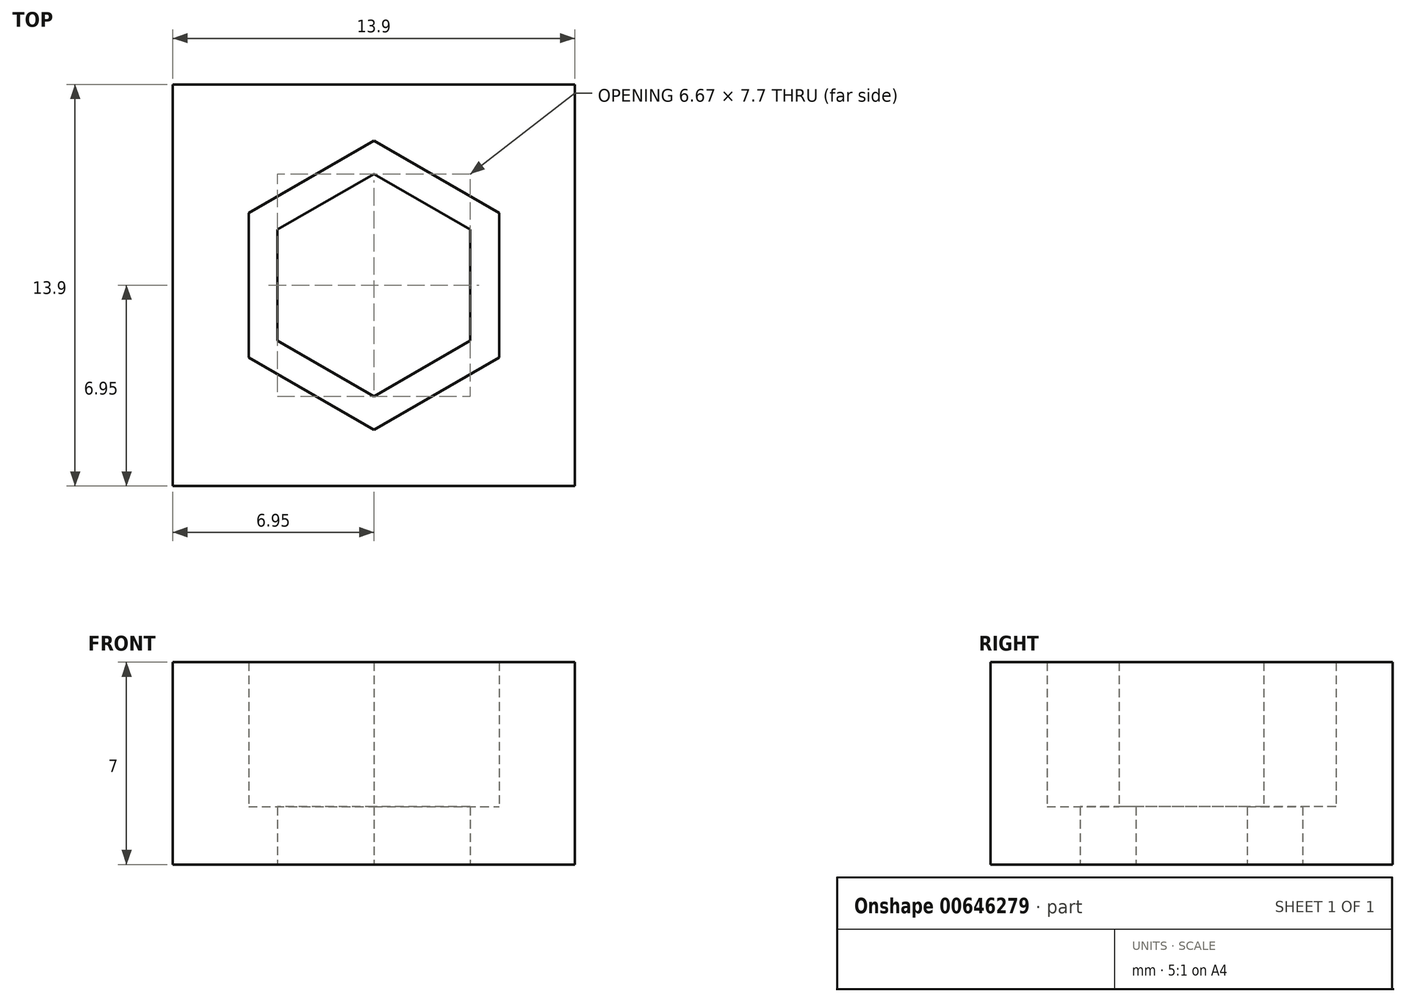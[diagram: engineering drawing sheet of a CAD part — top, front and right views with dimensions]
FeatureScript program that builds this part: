
annotation { "Feature Type Name" : "Feature", "Feature Type Description" : "" }
export const myFeature = defineFeature(function(context is Context, id is Id, definition is map)
    precondition{}
    {
        {
            var Q0;
            Q0=qCreatedBy(makeId("Top.planeOp"),FACE);
            var sketch = newSketch(context, id + "F0", { "sketchPlane" : qUnion([Q0])});
            skCircle(sketch, "E0", {"center": v(0, 0) * mm, "radius": 3.85 * mm});
            skLineSegment(sketch, "E1.bottom", {"start": v(6.95, 6.95) * mm, "end": v(-6.95, 6.95) * mm});
            skLineSegment(sketch, "E1.top", {"start": v(6.95, -6.95) * mm, "end": v(-6.95, -6.95) * mm});
            skLineSegment(sketch, "E1.left", {"start": v(6.95, 6.95) * mm, "end": v(6.95, -6.95) * mm});
            skLineSegment(sketch, "E1.right", {"start": v(-6.95, 6.95) * mm, "end": v(-6.95, -6.95) * mm});
            skCircle(sketch, "E2.cCircle", {"center": v(0, 0) * mm, "radius": 3.85 * mm, "construction": true});
            skLineSegment(sketch, "E2.0", {"start": v(0, 3.85) * mm, "end": v(3.33, 1.92) * mm});
            skLineSegment(sketch, "E2.1", {"start": v(3.33, 1.92) * mm, "end": v(3.33, -1.93) * mm});
            skLineSegment(sketch, "E2.2", {"start": v(3.33, -1.93) * mm, "end": v(0, -3.85) * mm});
            skLineSegment(sketch, "E2.3", {"start": v(0, -3.85) * mm, "end": v(-3.33, -1.92) * mm});
            skLineSegment(sketch, "E2.4", {"start": v(-3.33, -1.92) * mm, "end": v(-3.33, 1.93) * mm});
            skLineSegment(sketch, "E2.5", {"start": v(-3.33, 1.93) * mm, "end": v(0, 3.85) * mm});
            skSolve(sketch);
        }
        {
            var Q0;
            Q0=makeQuery(id+"F0.imprint","IMPRINT",FACE,{"disambiguationData":[TD([[makeQuery(id+"F0.imprint","IMPRINT",EDGE,{"derivedFrom":sQuery(id+"F0.wireOp",EDGE,"E1.bottom")}),1.0]])]});
            var Q1;
            {var subQ0=sQuery(id+"F0.wireOp",EDGE,"E2.3");Q1=makeQuery(id+"F0.imprint","IMPRINT",FACE,{"disambiguationData":[TD([[makeQuery(id+"F0.imprint","IMPRINT",EDGE,{"derivedFrom":subQ0}),1.0]])]});}
            var Q2;
            {var subQ0=sQuery(id+"F0.wireOp",EDGE,"E2.4");Q2=makeQuery(id+"F0.imprint","IMPRINT",FACE,{"disambiguationData":[TD([[makeQuery(id+"F0.imprint","IMPRINT",EDGE,{"derivedFrom":subQ0}),1.0]])]});}
            var Q3;
            {var subQ0=sQuery(id+"F0.wireOp",EDGE,"E2.5");Q3=makeQuery(id+"F0.imprint","IMPRINT",FACE,{"disambiguationData":[TD([[makeQuery(id+"F0.imprint","IMPRINT",EDGE,{"derivedFrom":subQ0}),1.0]])]});}
            var Q4;
            {var subQ0=sQuery(id+"F0.wireOp",EDGE,"E2.0");Q4=makeQuery(id+"F0.imprint","IMPRINT",FACE,{"disambiguationData":[TD([[makeQuery(id+"F0.imprint","IMPRINT",EDGE,{"derivedFrom":subQ0}),1.0]])]});}
            var Q5;
            {var subQ0=sQuery(id+"F0.wireOp",EDGE,"E2.1");Q5=makeQuery(id+"F0.imprint","IMPRINT",FACE,{"disambiguationData":[TD([[makeQuery(id+"F0.imprint","IMPRINT",EDGE,{"derivedFrom":subQ0}),1.0]])]});}
            var Q6;
            {var subQ0=sQuery(id+"F0.wireOp",EDGE,"E2.2");Q6=makeQuery(id+"F0.imprint","IMPRINT",FACE,{"disambiguationData":[TD([[makeQuery(id+"F0.imprint","IMPRINT",EDGE,{"derivedFrom":subQ0}),1.0]])]});}
            extrude(context, id + "F1", {"entities" : qUnion([Q0, Q1, Q2, Q3, Q4, Q5, Q6]), "depth" : 2 * mm, "offsetDistance" : 25 * mm});
        }
        {
            var Q0;
            Q0=makeQuery(id+"F1.opExtrude","CAP_FACE",FACE,{"disambiguationData":[OSD([sQuery(id+"F0.wireOp",EDGE,"E0"),sQuery(id+"F0.wireOp",EDGE,"E1.bottom"),sQuery(id+"F0.wireOp",EDGE,"E1.top"),sQuery(id+"F0.wireOp",EDGE,"E1.left"),sQuery(id+"F0.wireOp",EDGE,"E1.right")])],"isStart":false});
            var sketch = newSketch(context, id + "F2", { "sketchPlane" : qUnion([Q0])});
            skPoint(sketch, "E3.0", {"position": v(0, 0) * mm});
            skCircle(sketch, "E4", {"center": v(0, 0) * mm, "radius": 5 * mm});
            skLineSegment(sketch, "E5.bottom", {"start": v(6.95, 6.95) * mm, "end": v(-6.95, 6.95) * mm});
            skLineSegment(sketch, "E5.top", {"start": v(6.95, -6.95) * mm, "end": v(-6.95, -6.95) * mm});
            skLineSegment(sketch, "E5.left", {"start": v(6.95, 6.95) * mm, "end": v(6.95, -6.95) * mm});
            skLineSegment(sketch, "E5.right", {"start": v(-6.95, 6.95) * mm, "end": v(-6.95, -6.95) * mm});
            skCircle(sketch, "E6.cCircle", {"center": v(0, 0) * mm, "radius": 5 * mm, "construction": true});
            skLineSegment(sketch, "E6.0", {"start": v(0, 5) * mm, "end": v(4.33, 2.5) * mm});
            skLineSegment(sketch, "E6.1", {"start": v(4.33, 2.5) * mm, "end": v(4.33, -2.5) * mm});
            skLineSegment(sketch, "E6.2", {"start": v(4.33, -2.5) * mm, "end": v(0, -5) * mm});
            skLineSegment(sketch, "E6.3", {"start": v(0, -5) * mm, "end": v(-4.33, -2.5) * mm});
            skLineSegment(sketch, "E6.4", {"start": v(-4.33, -2.5) * mm, "end": v(-4.33, 2.5) * mm});
            skLineSegment(sketch, "E6.5", {"start": v(-4.33, 2.5) * mm, "end": v(0, 5) * mm});
            skSolve(sketch);
        }
        {
            var Q0;
            Q0=makeQuery(id+"F2.imprint","IMPRINT",FACE,{"disambiguationData":[TD([[makeQuery(id+"F2.imprint","IMPRINT",EDGE,{"derivedFrom":sQuery(id+"F2.wireOp",EDGE,"E4")}),-1.0]])]});
            var Q1;
            {var subQ0=sQuery(id+"F2.wireOp",EDGE,"E6.4");Q1=makeQuery(id+"F2.imprint","IMPRINT",FACE,{"disambiguationData":[TD([[makeQuery(id+"F2.imprint","IMPRINT",EDGE,{"derivedFrom":subQ0}),1.0]])]});}
            var Q2;
            {var subQ0=sQuery(id+"F2.wireOp",EDGE,"E6.5");Q2=makeQuery(id+"F2.imprint","IMPRINT",FACE,{"disambiguationData":[TD([[makeQuery(id+"F2.imprint","IMPRINT",EDGE,{"derivedFrom":subQ0}),1.0]])]});}
            var Q3;
            {var subQ0=sQuery(id+"F2.wireOp",EDGE,"E6.0");Q3=makeQuery(id+"F2.imprint","IMPRINT",FACE,{"disambiguationData":[TD([[makeQuery(id+"F2.imprint","IMPRINT",EDGE,{"derivedFrom":subQ0}),1.0]])]});}
            var Q4;
            {var subQ0=sQuery(id+"F2.wireOp",EDGE,"E6.1");Q4=makeQuery(id+"F2.imprint","IMPRINT",FACE,{"disambiguationData":[TD([[makeQuery(id+"F2.imprint","IMPRINT",EDGE,{"derivedFrom":subQ0}),1.0]])]});}
            var Q5;
            {var subQ0=sQuery(id+"F2.wireOp",EDGE,"E6.2");Q5=makeQuery(id+"F2.imprint","IMPRINT",FACE,{"disambiguationData":[TD([[makeQuery(id+"F2.imprint","IMPRINT",EDGE,{"derivedFrom":subQ0}),1.0]])]});}
            var Q6;
            {var subQ0=sQuery(id+"F2.wireOp",EDGE,"E6.3");Q6=makeQuery(id+"F2.imprint","IMPRINT",FACE,{"disambiguationData":[TD([[makeQuery(id+"F2.imprint","IMPRINT",EDGE,{"derivedFrom":subQ0}),1.0]])]});}
            extrude(context, id + "F3", {"entities" : qUnion([Q0, Q1, Q2, Q3, Q4, Q5, Q6]), "operationType" : NewBodyOperationType.ADD, "depth" : 5 * mm, "offsetDistance" : 25 * mm});
        }
    });
